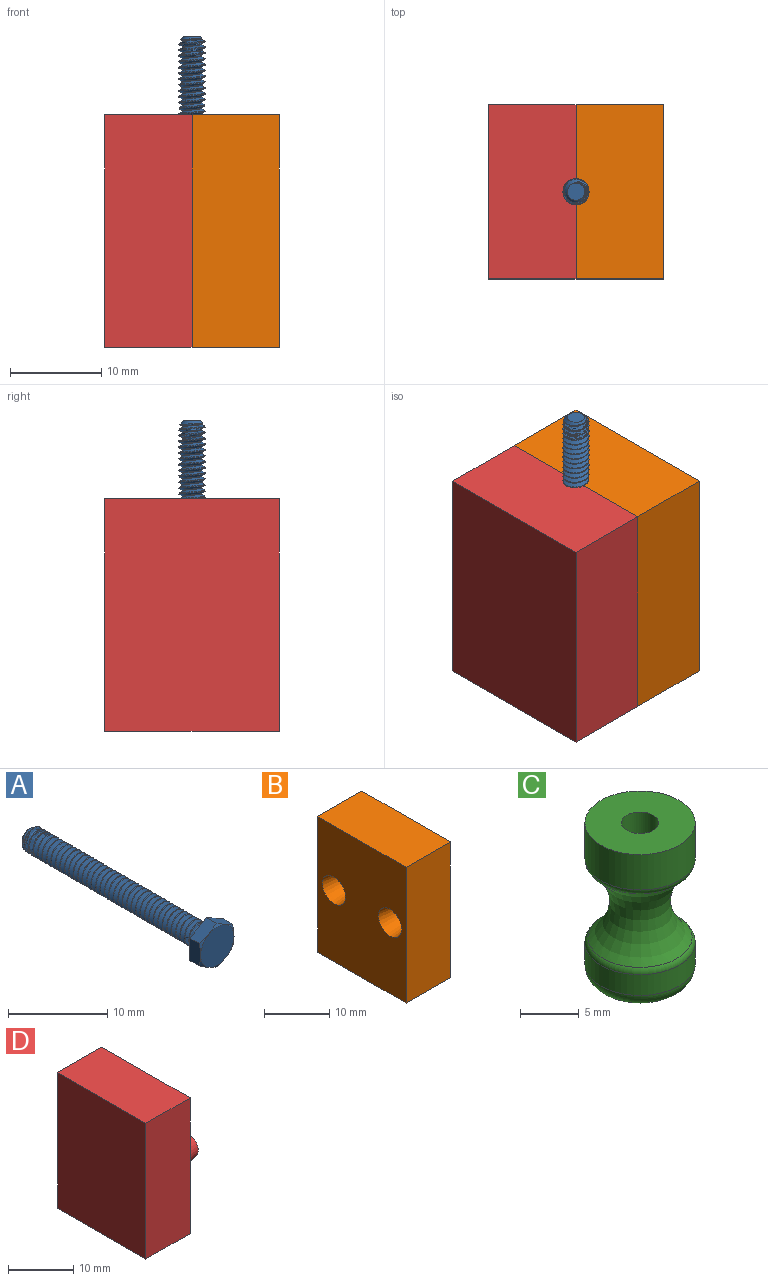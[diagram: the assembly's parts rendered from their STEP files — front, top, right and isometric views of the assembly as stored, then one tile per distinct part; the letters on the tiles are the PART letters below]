
ASSEMBLY  parts=4 mates=1
PART A: 21 faces, bbox 5.7x27.3x5.7 mm
  f0: plane 2.98x1.75mm, normal (-1,0,0), area 4mm2, adj f1,f5,f6,f16,f17
  f1: plane 2.61x1.75mm, normal (-0.5,0,-0.87), area 4mm2, adj f0,f2,f6,f15,f16
  f2: plane 2.61x1.75mm, normal (0.5,0,-0.87), area 4mm2, adj f1,f3,f6,f14,f15
  f3: plane 2.98x1.75mm, normal (1,0,0), area 4mm2, adj f2,f4,f6,f14,f19
  f4: plane 2.61x1.75mm, normal (0.5,0,0.87), area 4mm2, adj f3,f5,f6,f18,f19
  f5: plane 2.61x1.75mm, normal (-0.5,0,0.87), area 4mm2, adj f0,f4,f6,f17,f18
  f6: plane 5.73x5mm, normal (0,1,0), area 14.9mm2, adj f0,f1,f2,f3,f4,f5,f7,f11
  f7: cylinder r=1.42mm len=24.92mm, axis (0,-1,0), area 47.3mm2, adj f6,f8,f9,f11,f13
  f8: cone r=1.42mm half-angle=45deg, axis (0,-1,0), area 2.8mm2, adj f7,f9,f10,f11,f12,f13
  f9: cone r=1.42mm half-angle=45deg, axis (0,-1,0), area 0mm2, adj f7,f8,f13
  f10: plane 1.89x1.89mm, normal (0,1,0), area 2.8mm2, adj f8
  f11: bspline ~25.85x3.33mm, area 142mm2, adj f6,f7,f8,f12
  f12: cylinder r=1.01mm len=25.33mm, axis (0,-1,0), area 15.1mm2, adj f6,f8,f11,f13
  f13: bspline ~25.56x2.84mm, area 141.8mm2, adj f6,f7,f8,f9,f12
  f14: cone r=2.38mm half-angle=60deg, axis (0,1,0), area 0.6mm2, adj f2,f3,f20
  f15: cone r=2.38mm half-angle=60deg, axis (0,1,0), area 0.6mm2, adj f1,f2,f20
  f16: cone r=2.38mm half-angle=60deg, axis (0,1,0), area 0.6mm2, adj f0,f1,f20
  f17: cone r=2.38mm half-angle=60deg, axis (0,1,0), area 0.6mm2, adj f0,f5,f20
  f18: cone r=2.38mm half-angle=60deg, axis (0,1,0), area 0.6mm2, adj f4,f5,f20
  f19: cone r=2.38mm half-angle=60deg, axis (0,1,0), area 0.6mm2, adj f3,f4,f20
  f20: plane 4.76x4.76mm, normal (0,-1,0), area 17.8mm2, adj f14,f15,f16,f17,f18,f19
PART B: 10 faces, bbox 9.5x19.1x25.4 mm
  f0: plane 25.4x19.05mm, normal (1,0,0), area 483.9mm2, adj f1,f2,f3,f4
  f1: plane 19.05x9.53mm, normal (0,0,1), area 181.5mm2, adj f0,f3,f4,f5
  f2: plane 19.05x9.53mm, normal (0,0,-1), area 181.5mm2, adj f0,f3,f4,f5
  f3: plane 25.4x9.53mm, normal (0,-1,0), area 241.9mm2, adj f0,f1,f2,f5
  f4: plane 25.4x9.53mm, normal (0,1,0), area 241.9mm2, adj f0,f1,f2,f5
  f5: plane 25.4x19.05mm, normal (-1,0,0), area 444.6mm2, adj f1,f2,f3,f4,f6,f8
  f6: cone r=2.05mm half-angle=8deg, axis (-1,0,0), area 45.9mm2, adj f5,f7
  f7: plane 4.11x4.11mm, normal (-1,0,0), area 13.3mm2, adj f6
  f8: cone r=2.05mm half-angle=8deg, axis (-1,0,0), area 45.9mm2, adj f5,f9
  f9: plane 4.11x4.11mm, normal (-1,0,0), area 13.3mm2, adj f8
PART C: 12 faces, bbox 10.2x10.2x16.2 mm
  f0: plane 6.35x6.35mm, normal (0,0,1), area 31.7mm2, adj f11
  f1: plane 6.35x6.35mm, normal (0,0,-1), area 31.7mm2, adj f2
  f2: torus R=3.17mm, axis (0,0,1), area 62.3mm2, adj f1,f3
  f3: cylinder r=4.7mm len=9.4mm, axis (0,0,1), area 63.9mm2, adj f2,f4
  f4: torus R=3.94mm, axis (0,0,1), area 18.9mm2, adj f3,f5
  f5: revolved ~8.87x8.87mm, area 178.6mm2, adj f4,f6
  f6: torus R=3.94mm, axis (0,0,1), area 18.9mm2, adj f5,f7
  f7: cylinder r=4.7mm len=9.4mm, axis (0,0,1), area 108.9mm2, adj f6,f8
  f8: plane 9.4x9.4mm, normal (0,0,1), area 61.5mm2, adj f7,f9
  f9: cylinder r=1.59mm len=13.69mm, axis (0,0,1), area 136.5mm2, adj f8,f10
  f10: plane 6.35x6.35mm, normal (0,0,-1), area 23.8mm2, adj f9,f11
  f11: cylinder r=3.17mm len=6.35mm, axis (0,0,1), area 30.4mm2, adj f0,f10
PART D: 10 faces, bbox 12.7x19.1x25.4 mm
  f0: plane 25.4x9.53mm, normal (0,1,0), area 241.9mm2, adj f2,f3,f4,f5
  f1: plane 25.4x9.53mm, normal (0,-1,0), area 241.9mm2, adj f2,f3,f4,f5
  f2: plane 19.05x9.53mm, normal (0,0,1), area 181.5mm2, adj f0,f1,f4,f5
  f3: plane 19.05x9.53mm, normal (0,0,-1), area 181.5mm2, adj f0,f1,f4,f5
  f4: plane 25.4x19.05mm, normal (-1,0,0), area 483.9mm2, adj f0,f1,f2,f3
  f5: plane 25.4x19.05mm, normal (1,0,0), area 444.6mm2, adj f0,f1,f2,f3,f6,f8
  f6: cone r=2.5mm half-angle=8deg, axis (-1,0,0), area 45.9mm2, adj f5,f7
  f7: plane 4.11x4.11mm, normal (1,0,0), area 13.3mm2, adj f6
  f8: cone r=2.5mm half-angle=8deg, axis (-1,0,0), area 45.9mm2, adj f5,f9
  f9: plane 4.11x4.11mm, normal (1,0,0), area 13.3mm2, adj f8
PLACE A rot(axis=(1,0,0),90deg) t=(-0.82,4.08,8.55)mm
PLACE B t=(-0.82,4.08,0)mm
PLACE C t=(-0.82,1.54,-15.32)mm
PLACE D t=(-0.82,4.08,0)mm
MATE fastened D.f5 <-> B.f5  axis (1,0,0) through (-0.82,4.08,0)mm
